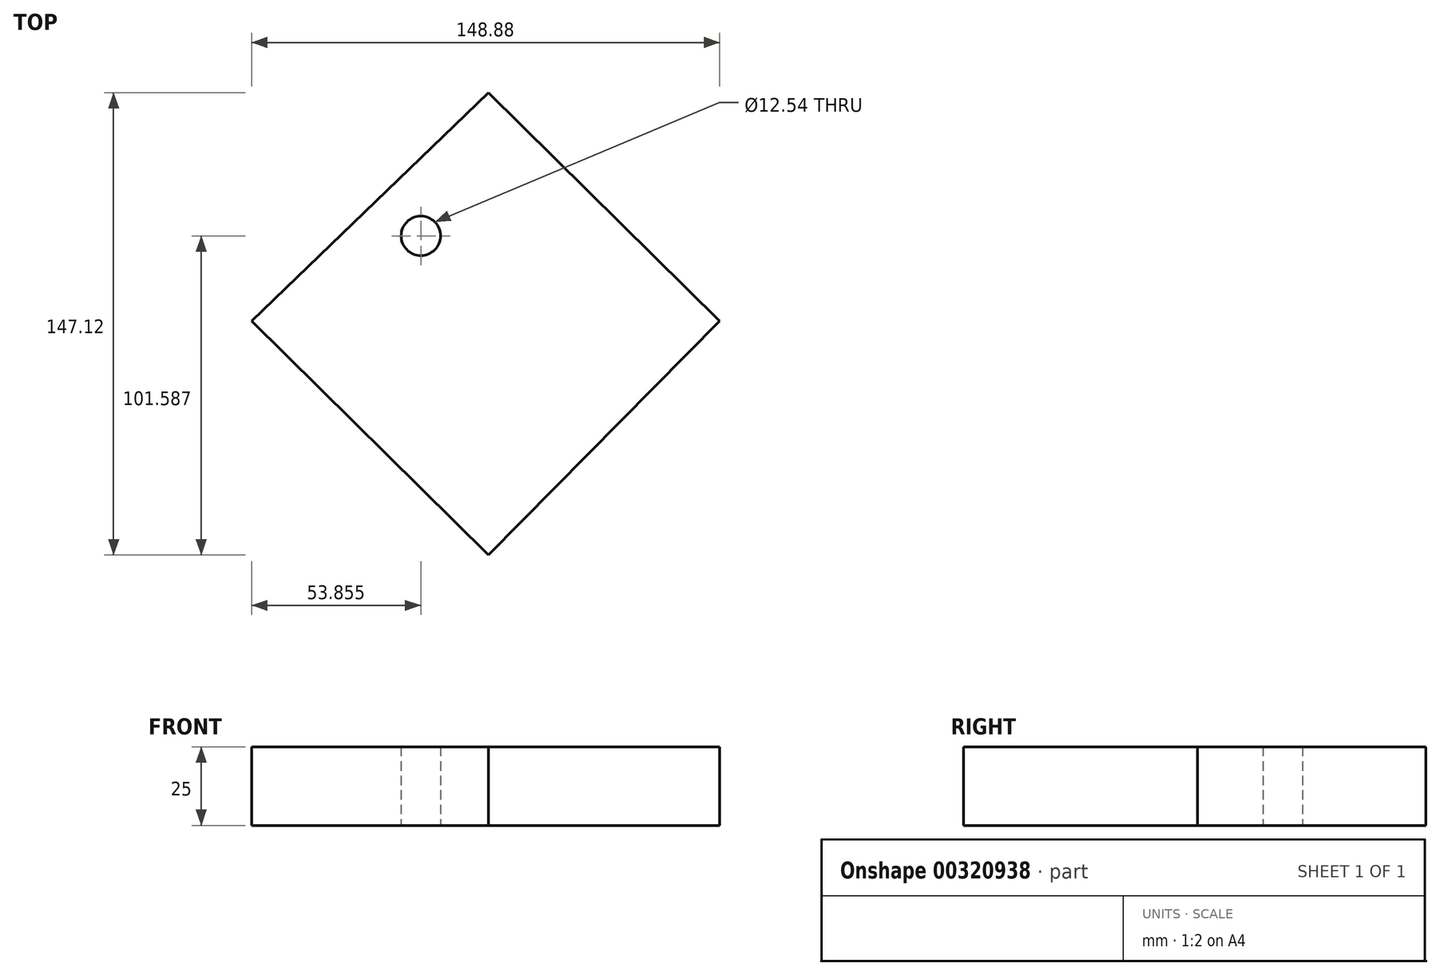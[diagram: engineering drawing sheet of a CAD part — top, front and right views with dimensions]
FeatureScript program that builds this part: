
annotation { "Feature Type Name" : "Feature", "Feature Type Description" : "" }
export const myFeature = defineFeature(function(context is Context, id is Id, definition is map)
    precondition{}
    {
        {
            var Q0;
            Q0=qCreatedBy(makeId("Top.planeOp"),FACE);
            var sketch = newSketch(context, id + "F0", { "sketchPlane" : qUnion([Q0])});
            skLineSegment(sketch, "E0", {"start": v(0, 72.68) * mm, "end": v(-75.31, 0) * mm});
            skLineSegment(sketch, "E1", {"start": v(-75.31, 0) * mm, "end": v(0, -74.44) * mm});
            skLineSegment(sketch, "E2", {"start": v(0, -74.44) * mm, "end": v(73.57, 0) * mm});
            skLineSegment(sketch, "E3", {"start": v(0, 72.68) * mm, "end": v(73.57, 0) * mm});
            skCircle(sketch, "E4", {"center": v(-21.45, 27.15) * mm, "radius": 6.27 * mm});
            skSolve(sketch);
        }
        {
            var Q0;
            Q0 = qSketchRegion(id + "F0", true);
            extrude(context, id + "F1", {"entities" : qUnion([Q0]), "depth" : 25 * mm});
        }
    });
